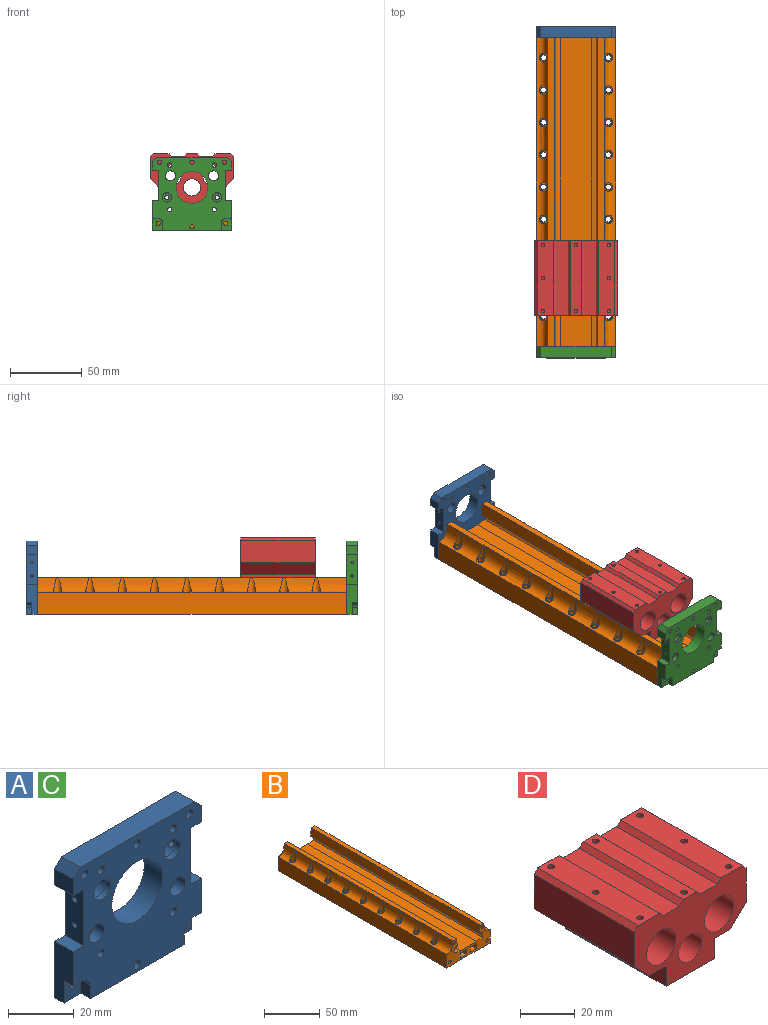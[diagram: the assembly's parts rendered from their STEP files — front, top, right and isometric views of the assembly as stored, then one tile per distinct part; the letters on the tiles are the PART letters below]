
ASSEMBLY  parts=4 mates=3
PART A: 53 faces, bbox 55x8x51 mm
  f0: cylinder r=3.25mm len=6.5mm, axis (0,-1,0), area 81mm2, adj f1,f19,f28,f29
  f1: plane 6.5x6.5mm, normal (0,-1,0), area 25.9mm2, adj f0,f5,f28,f29
  f2: cylinder r=4mm len=8mm, axis (0,1,0), area 148.1mm2, adj f20,f26,f27
  f3: plane 55x8mm, normal (0,0,-1), area 382mm2, adj f4,f19,f20,f23,f25,f33,f46,f48
  f4: plane 21x8mm, normal (1,0,0), area 135mm2, adj f3,f8,f19,f20,f24,f25
  f5: cylinder r=1.5mm len=4mm, axis (0,1,0), area 37.7mm2, adj f1,f20
  f6: cylinder r=1.5mm len=4mm, axis (0,1,0), area 37.7mm2, adj f20,f25
  f7: cylinder r=1.5mm len=8mm, axis (0,1,0), area 75.4mm2, adj f19,f20
  f8: plane 8x4.5mm, normal (0,0,1), area 36mm2, adj f4,f9,f19,f20
  f9: plane 21x8mm, normal (1,0,0), area 163.2mm2, adj f8,f10,f19,f20,f27,f29
  f10: plane 8x4.5mm, normal (0,0,-1), area 36mm2, adj f9,f11,f19,f20
  f11: plane 8x6mm, normal (1,0,0), area 48mm2, adj f10,f19,f20,f21
  f12: plane 49x8mm, normal (0,0,1), area 392mm2, adj f19,f20,f21,f44
  f13: cylinder r=1.5mm len=8mm, axis (0,1,0), area 75.4mm2, adj f19,f20
  f14: cylinder r=11mm len=22mm, axis (0,1,0), area 552.9mm2, adj f19,f20
  f15: cylinder r=1.5mm len=8mm, axis (0,1,0), area 75.4mm2, adj f19,f20
  f16: cylinder r=1.5mm len=8mm, axis (0,1,0), area 75.4mm2, adj f19,f20
  f17: cylinder r=1.5mm len=8mm, axis (0,1,0), area 75.4mm2, adj f19,f20
  f18: cylinder r=3.5mm len=7mm, axis (0,1,0), area 44mm2, adj f19,f26
  f19: plane 55x51mm, normal (0,-1,0), area 1911.9mm2, adj f0,f3,f4,f7,f8,f9,f10,f11
  f20: plane 55x51mm, normal (0,1,0), area 2041.5mm2, adj f2,f3,f4,f5,f6,f7,f8,f9
  f21: plane 8x3mm, normal (0.71,0,0.71), area 33.9mm2, adj f11,f12,f19,f20
  f22: cylinder r=3.25mm len=4mm, axis (0,-1,0), area 20.4mm2, adj f19,f23,f24,f25
  f23: plane 5x4mm, normal (1,0,0), area 20mm2, adj f3,f19,f22,f25
  f24: plane 4x4mm, normal (0,0,-1), area 16mm2, adj f4,f19,f22,f25
  f25: plane 8.25x7.25mm, normal (0,-1,0), area 50.5mm2, adj f3,f4,f6,f22,f23,f24
  f26: plane 8x8mm, normal (0,1,0), area 11.8mm2, adj f2,f18
  f27: cylinder r=0.88mm len=4.98mm, axis (1,0,0), area 24.6mm2, adj f2,f9
  f28: cone r=0mm half-angle=59deg, axis (1,0,0), area 2.6mm2, adj f0,f1,f29
  f29: cylinder r=0.88mm len=5mm, axis (1,0,0), area 26.9mm2, adj f0,f1,f9,f28
  f30: cylinder r=3.25mm len=6.5mm, axis (0,-1,0), area 81mm2, adj f19,f31,f51,f52
  f31: plane 6.5x6.5mm, normal (0,-1,0), area 25.9mm2, adj f30,f34,f51,f52
  f32: cylinder r=4mm len=8mm, axis (0,1,0), area 148.1mm2, adj f20,f49,f50
  f33: plane 21x8mm, normal (-1,0,0), area 135mm2, adj f3,f19,f20,f36,f47,f48
  f34: cylinder r=1.5mm len=4mm, axis (0,1,0), area 37.7mm2, adj f20,f31
  f35: cylinder r=1.5mm len=4mm, axis (0,1,0), area 37.7mm2, adj f20,f48
  f36: plane 8x4.5mm, normal (0,0,1), area 36mm2, adj f19,f20,f33,f37
  f37: plane 21x8mm, normal (-1,0,0), area 163.2mm2, adj f19,f20,f36,f38,f50,f52
  f38: plane 8x4.5mm, normal (0,0,-1), area 36mm2, adj f19,f20,f37,f39
  f39: plane 8x6mm, normal (-1,0,0), area 48mm2, adj f19,f20,f38,f44
  f40: cylinder r=1.5mm len=8mm, axis (0,1,0), area 75.4mm2, adj f19,f20
  f41: cylinder r=1.5mm len=8mm, axis (0,1,0), area 75.4mm2, adj f19,f20
  f42: cylinder r=1.5mm len=8mm, axis (0,1,0), area 75.4mm2, adj f19,f20
  f43: cylinder r=3.5mm len=7mm, axis (0,1,0), area 44mm2, adj f19,f49
  f44: plane 8x3mm, normal (-0.71,0,0.71), area 33.9mm2, adj f12,f19,f20,f39
  f45: cylinder r=3.25mm len=4mm, axis (0,-1,0), area 20.4mm2, adj f19,f46,f47,f48
  f46: plane 5x4mm, normal (-1,0,0), area 20mm2, adj f3,f19,f45,f48
  f47: plane 4x4mm, normal (0,0,-1), area 16mm2, adj f19,f33,f45,f48
  f48: plane 8.25x7.25mm, normal (0,-1,0), area 50.5mm2, adj f3,f33,f35,f45,f46,f47
  f49: plane 8x8mm, normal (0,1,0), area 11.8mm2, adj f32,f43
  f50: cylinder r=0.88mm len=4.98mm, axis (-1,0,0), area 24.6mm2, adj f32,f37
  f51: cone r=0mm half-angle=59deg, axis (-1,0,0), area 2.6mm2, adj f30,f31,f52
  f52: cylinder r=0.88mm len=5mm, axis (-1,0,0), area 26.9mm2, adj f30,f31,f37,f51
PART B: 142 faces, bbox 55x215x26 mm
  f0: cylinder r=3mm len=11mm, axis (0,0,-1), area 59.8mm2, adj f10,f46
  f1: cylinder r=3mm len=11mm, axis (0,0,-1), area 59.8mm2, adj f10,f45
  f2: cylinder r=3mm len=11mm, axis (0,0,-1), area 59.8mm2, adj f10,f43
  f3: cylinder r=3mm len=11mm, axis (0,0,-1), area 59.8mm2, adj f10,f41
  f4: cylinder r=3mm len=11mm, axis (0,0,-1), area 59.8mm2, adj f10,f39
  f5: cylinder r=3mm len=11mm, axis (0,0,-1), area 59.8mm2, adj f10,f37
  f6: cylinder r=3mm len=11mm, axis (0,0,-1), area 59.8mm2, adj f10,f35
  f7: cylinder r=3mm len=11mm, axis (0,0,-1), area 59.8mm2, adj f10,f33
  f8: cylinder r=3mm len=11mm, axis (0,0,-1), area 59.8mm2, adj f10,f29
  f9: cylinder r=1.5mm len=19.34mm, axis (0,1,0), area 173.6mm2, adj f27,f48
  f10: extruded ~215x11mm, area 2852.4mm2, adj f0,f1,f2,f3,f4,f5,f6,f7
  f11: plane 215x4.5mm, normal (0,0,1), area 967.5mm2, adj f10,f12,f27,f28
  f12: plane 215x8.5mm, normal (-0.99,0,0.12), area 1840.1mm2, adj f11,f13,f27,f28
  f13: plane 215x0.91mm, normal (0,0,-1), area 195.8mm2, adj f12,f14,f27,f28
  f14: cylinder r=3.56mm len=215mm, axis (0,1,0), area 1780.3mm2, adj f13,f15,f27,f28
  f15: plane 215x7mm, normal (-0.14,0,0.99), area 1520.3mm2, adj f14,f16,f27,f28
  f16: plane 215x21mm, normal (0,0,1), area 4515mm2, adj f15,f27,f28,f64
  f17: plane 215x35mm, normal (0,0,-1), area 7525mm2, adj f18,f27,f28,f65
  f18: plane 215x0.5mm, normal (-1,0,0), area 107.5mm2, adj f17,f19,f27,f28
  f19: plane 215x10mm, normal (0,0,-1), area 2036.9mm2, adj f18,f26,f27,f28,f30,f32,f34,f36
  f20: plane 215x6mm, normal (-1,0,0), area 1290mm2, adj f21,f23,f27,f28
  f21: plane 215x8mm, normal (0,0,1), area 1720mm2, adj f20,f22,f27,f28
  f22: plane 215x6mm, normal (1,0,0), area 1290mm2, adj f21,f23,f27,f28
  f23: plane 215x8mm, normal (0,0,-1), area 1720mm2, adj f20,f22,f27,f28
  f24: cylinder r=1.5mm len=215mm, axis (0,1,0), area 2026.3mm2, adj f27,f28
  f25: cylinder r=1.5mm len=12.34mm, axis (0,1,0), area 107.6mm2, adj f28,f31
  f26: plane 215x15mm, normal (1,0,0), area 3225mm2, adj f10,f19,f27,f28
  f27: plane 55x26mm, normal (0,-1,0), area 652.7mm2, adj f9,f10,f11,f12,f13,f14,f15,f16
  f28: plane 55x26mm, normal (0,1,0), area 652.7mm2, adj f10,f11,f12,f13,f14,f15,f16,f17
  f29: plane 6x6mm, normal (0,0,1), area 15.7mm2, adj f8,f30
  f30: cylinder r=2mm len=15mm, axis (0,0,-1), area 188.5mm2, adj f19,f29
  f31: cylinder r=3mm len=3mm, axis (0,0,-1), area 8mm2, adj f25
  f32: cylinder r=2mm len=15mm, axis (0,0,-1), area 188.5mm2, adj f19,f33
  f33: plane 6x6mm, normal (0,0,1), area 15.7mm2, adj f7,f32
  f34: cylinder r=2mm len=15mm, axis (0,0,-1), area 188.5mm2, adj f19,f35
  f35: plane 6x6mm, normal (0,0,1), area 15.7mm2, adj f6,f34
  f36: cylinder r=2mm len=15mm, axis (0,0,-1), area 188.5mm2, adj f19,f37
  f37: plane 6x6mm, normal (0,0,1), area 15.7mm2, adj f5,f36
  f38: cylinder r=2mm len=15mm, axis (0,0,-1), area 188.5mm2, adj f19,f39
  f39: plane 6x6mm, normal (0,0,1), area 15.7mm2, adj f4,f38
  f40: cylinder r=2mm len=15mm, axis (0,0,-1), area 188.5mm2, adj f19,f41
  f41: plane 6x6mm, normal (0,0,1), area 15.7mm2, adj f3,f40
  f42: cylinder r=2mm len=15mm, axis (0,0,-1), area 188.5mm2, adj f19,f43
  f43: plane 6x6mm, normal (0,0,1), area 15.7mm2, adj f2,f42
  f44: cylinder r=2mm len=15mm, axis (0,0,-1), area 188.5mm2, adj f19,f45
  f45: plane 6x6mm, normal (0,0,1), area 15.7mm2, adj f1,f44
  f46: plane 6x6mm, normal (0,0,1), area 15.7mm2, adj f0,f47
  f47: cylinder r=2mm len=15mm, axis (0,0,-1), area 188.5mm2, adj f19,f46
  f48: cylinder r=3mm len=3mm, axis (0,0,-1), area 8mm2, adj f9
  f49: cylinder r=3mm len=11mm, axis (0,0,-1), area 59.8mm2, adj f59,f91
  f50: cylinder r=3mm len=11mm, axis (0,0,-1), area 59.8mm2, adj f59,f90
  f51: cylinder r=3mm len=11mm, axis (0,0,-1), area 59.8mm2, adj f59,f88
  f52: cylinder r=3mm len=11mm, axis (0,0,-1), area 59.8mm2, adj f59,f86
  f53: cylinder r=3mm len=11mm, axis (0,0,-1), area 59.8mm2, adj f59,f84
  f54: cylinder r=3mm len=11mm, axis (0,0,-1), area 59.8mm2, adj f59,f82
  f55: cylinder r=3mm len=11mm, axis (0,0,-1), area 59.8mm2, adj f59,f80
  f56: cylinder r=3mm len=11mm, axis (0,0,-1), area 59.8mm2, adj f59,f78
  f57: cylinder r=3mm len=11mm, axis (0,0,-1), area 59.8mm2, adj f59,f74
  f58: cylinder r=1.5mm len=19.34mm, axis (0,1,0), area 173.6mm2, adj f27,f93
  f59: extruded ~215x11mm, area 2852.4mm2, adj f27,f28,f49,f50,f51,f52,f53,f54
  f60: plane 215x4.5mm, normal (0,0,1), area 967.5mm2, adj f27,f28,f59,f61
  f61: plane 215x8.5mm, normal (0.99,0,0.12), area 1840.1mm2, adj f27,f28,f60,f62
  f62: plane 215x0.91mm, normal (0,0,-1), area 195.8mm2, adj f27,f28,f61,f63
  f63: cylinder r=3.56mm len=215mm, axis (0,1,0), area 1780.3mm2, adj f27,f28,f62,f64
  f64: plane 215x7mm, normal (0.14,0,0.99), area 1520.3mm2, adj f16,f27,f28,f63
  f65: plane 215x0.5mm, normal (1,0,0), area 107.5mm2, adj f17,f27,f28,f66
  f66: plane 215x10mm, normal (0,0,-1), area 2036.9mm2, adj f27,f28,f65,f73,f75,f77,f79,f81
  f67: plane 215x6mm, normal (1,0,0), area 1290mm2, adj f27,f28,f68,f70
  f68: plane 215x8mm, normal (0,0,1), area 1720mm2, adj f27,f28,f67,f69
  f69: plane 215x6mm, normal (-1,0,0), area 1290mm2, adj f27,f28,f68,f70
  f70: plane 215x8mm, normal (0,0,-1), area 1720mm2, adj f27,f28,f67,f69
  f71: cylinder r=1.5mm len=215mm, axis (0,1,0), area 2026.3mm2, adj f27,f28
  f72: cylinder r=1.5mm len=12.34mm, axis (0,1,0), area 107.6mm2, adj f28,f76
  f73: plane 215x15mm, normal (-1,0,0), area 3225mm2, adj f27,f28,f59,f66
  f74: plane 6x6mm, normal (0,0,1), area 15.7mm2, adj f57,f75
  f75: cylinder r=2mm len=15mm, axis (0,0,-1), area 188.5mm2, adj f66,f74
  f76: cylinder r=3mm len=3mm, axis (0,0,-1), area 8mm2, adj f72
  f77: cylinder r=2mm len=15mm, axis (0,0,-1), area 188.5mm2, adj f66,f78
  f78: plane 6x6mm, normal (0,0,1), area 15.7mm2, adj f56,f77
  f79: cylinder r=2mm len=15mm, axis (0,0,-1), area 188.5mm2, adj f66,f80
  f80: plane 6x6mm, normal (0,0,1), area 15.7mm2, adj f55,f79
  f81: cylinder r=2mm len=15mm, axis (0,0,-1), area 188.5mm2, adj f66,f82
  f82: plane 6x6mm, normal (0,0,1), area 15.7mm2, adj f54,f81
  f83: cylinder r=2mm len=15mm, axis (0,0,-1), area 188.5mm2, adj f66,f84
  f84: plane 6x6mm, normal (0,0,1), area 15.7mm2, adj f53,f83
  f85: cylinder r=2mm len=15mm, axis (0,0,-1), area 188.5mm2, adj f66,f86
  f86: plane 6x6mm, normal (0,0,1), area 15.7mm2, adj f52,f85
  f87: cylinder r=2mm len=15mm, axis (0,0,-1), area 188.5mm2, adj f66,f88
  f88: plane 6x6mm, normal (0,0,1), area 15.7mm2, adj f51,f87
  f89: cylinder r=2mm len=15mm, axis (0,0,-1), area 188.5mm2, adj f66,f90
  f90: plane 6x6mm, normal (0,0,1), area 15.7mm2, adj f50,f89
  f91: plane 6x6mm, normal (0,0,1), area 15.7mm2, adj f49,f92
  f92: cylinder r=2mm len=15mm, axis (0,0,-1), area 188.5mm2, adj f66,f91
  f93: cylinder r=3mm len=3mm, axis (0,0,-1), area 8mm2, adj f58
  f94: cylinder r=3mm len=3mm, axis (0,0,-1), area 8mm2, adj f96
  f95: cylinder r=3mm len=3mm, axis (0,0,-1), area 8mm2, adj f96
  f96: cylinder r=1.5mm len=19.18mm, axis (0,1,0), area 163.4mm2, adj f94,f95
  f97: cylinder r=3mm len=3mm, axis (0,0,-1), area 8mm2, adj f99
  f98: cylinder r=3mm len=3mm, axis (0,0,-1), area 8mm2, adj f99
  f99: cylinder r=1.5mm len=19.18mm, axis (0,1,0), area 163.4mm2, adj f97,f98
  f100: cylinder r=3mm len=3mm, axis (0,0,-1), area 8mm2, adj f102
  f101: cylinder r=3mm len=3mm, axis (0,0,-1), area 8mm2, adj f102
  f102: cylinder r=1.5mm len=19.18mm, axis (0,1,0), area 163.4mm2, adj f100,f101
  f103: cylinder r=3mm len=3mm, axis (0,0,-1), area 8mm2, adj f105
  f104: cylinder r=3mm len=3mm, axis (0,0,-1), area 8mm2, adj f105
  f105: cylinder r=1.5mm len=19.18mm, axis (0,1,0), area 163.4mm2, adj f103,f104
  f106: cylinder r=3mm len=3mm, axis (0,0,-1), area 8mm2, adj f108
  f107: cylinder r=3mm len=3mm, axis (0,0,-1), area 8mm2, adj f108
  f108: cylinder r=1.5mm len=19.18mm, axis (0,1,0), area 163.4mm2, adj f106,f107
  f109: cylinder r=3mm len=3mm, axis (0,0,-1), area 8mm2, adj f111
  f110: cylinder r=3mm len=3mm, axis (0,0,-1), area 8mm2, adj f111
  f111: cylinder r=1.5mm len=19.18mm, axis (0,1,0), area 163.4mm2, adj f109,f110
  f112: cylinder r=3mm len=3mm, axis (0,0,-1), area 8mm2, adj f114
  f113: cylinder r=3mm len=3mm, axis (0,0,-1), area 8mm2, adj f114
  f114: cylinder r=1.5mm len=19.18mm, axis (0,1,0), area 163.4mm2, adj f112,f113
  f115: cylinder r=3mm len=3mm, axis (0,0,-1), area 8mm2, adj f117
  f116: cylinder r=3mm len=3mm, axis (0,0,-1), area 8mm2, adj f117
  f117: cylinder r=1.5mm len=19.18mm, axis (0,1,0), area 163.4mm2, adj f115,f116
  f118: cylinder r=3mm len=3mm, axis (0,0,-1), area 8mm2, adj f120
  f119: cylinder r=3mm len=3mm, axis (0,0,-1), area 8mm2, adj f120
  f120: cylinder r=1.5mm len=19.18mm, axis (0,1,0), area 163.4mm2, adj f118,f119
  f121: cylinder r=3mm len=3mm, axis (0,0,-1), area 8mm2, adj f123
  f122: cylinder r=3mm len=3mm, axis (0,0,-1), area 8mm2, adj f123
  f123: cylinder r=1.5mm len=19.18mm, axis (0,1,0), area 163.4mm2, adj f121,f122
  f124: cylinder r=3mm len=3mm, axis (0,0,-1), area 8mm2, adj f126
  f125: cylinder r=3mm len=3mm, axis (0,0,-1), area 8mm2, adj f126
  f126: cylinder r=1.5mm len=19.18mm, axis (0,1,0), area 163.4mm2, adj f124,f125
  f127: cylinder r=3mm len=3mm, axis (0,0,-1), area 8mm2, adj f129
  f128: cylinder r=3mm len=3mm, axis (0,0,-1), area 8mm2, adj f129
  f129: cylinder r=1.5mm len=19.18mm, axis (0,1,0), area 163.4mm2, adj f127,f128
  f130: cylinder r=3mm len=3mm, axis (0,0,-1), area 8mm2, adj f132
  f131: cylinder r=3mm len=3mm, axis (0,0,-1), area 8mm2, adj f132
  f132: cylinder r=1.5mm len=19.18mm, axis (0,1,0), area 163.4mm2, adj f130,f131
  f133: cylinder r=3mm len=3mm, axis (0,0,-1), area 8mm2, adj f135
  f134: cylinder r=3mm len=3mm, axis (0,0,-1), area 8mm2, adj f135
  f135: cylinder r=1.5mm len=19.18mm, axis (0,1,0), area 163.4mm2, adj f133,f134
  f136: cylinder r=3mm len=3mm, axis (0,0,-1), area 8mm2, adj f138
  f137: cylinder r=3mm len=3mm, axis (0,0,-1), area 8mm2, adj f138
  f138: cylinder r=1.5mm len=19.18mm, axis (0,1,0), area 163.4mm2, adj f136,f137
  f139: cylinder r=3mm len=3mm, axis (0,0,-1), area 8mm2, adj f141
  f140: cylinder r=3mm len=3mm, axis (0,0,-1), area 8mm2, adj f141
  f141: cylinder r=1.5mm len=19.18mm, axis (0,1,0), area 163.4mm2, adj f139,f140
PART C: same geometry as A
PART D: 41 faces, bbox 58x52x34.5 mm
  f0: plane 52x7mm, normal (0,0,1), area 354.2mm2, adj f9,f10,f14,f22,f24,f34
  f1: cylinder r=6mm len=52mm, axis (0,1,0), area 1960.4mm2, adj f9,f10
  f2: plane 52x25mm, normal (0,0,-1), area 1300mm2, adj f3,f9,f10,f25
  f3: plane 52x9mm, normal (1,0,0), area 468mm2, adj f2,f4,f9,f10
  f4: plane 52x8.5mm, normal (0,0,-1), area 442mm2, adj f3,f9,f10,f11
  f5: plane 52x15.5mm, normal (1,0,0), area 806mm2, adj f9,f10,f11,f12
  f6: plane 52x11mm, normal (0,0,1), area 557.3mm2, adj f9,f10,f12,f13,f16,f18,f20
  f7: plane 52x8.5mm, normal (0,0,1), area 442mm2, adj f9,f10,f13,f14
  f8: cylinder r=7.5mm len=52mm, axis (0,1,0), area 2450.4mm2, adj f9,f10
  f9: plane 58x34.5mm, normal (0,-1,0), area 1127.5mm2, adj f0,f1,f2,f3,f4,f5,f6,f7
  f10: plane 58x34.5mm, normal (0,1,0), area 1127.5mm2, adj f0,f1,f2,f3,f4,f5,f6,f7
  f11: plane 52x8mm, normal (0.71,0,-0.71), area 588.3mm2, adj f4,f5,f9,f10
  f12: plane 52x2mm, normal (0.71,0,0.71), area 147.1mm2, adj f5,f6,f9,f10
  f13: plane 52x2mm, normal (-0.71,0,0.71), area 147.1mm2, adj f6,f7,f9,f10
  f14: plane 52x2mm, normal (0.71,0,0.71), area 147.1mm2, adj f0,f7,f9,f10
  f15: cone r=0mm half-angle=59deg, axis (0,0,1), area 5.7mm2, adj f16
  f16: cylinder r=1.25mm len=10.75mm, axis (0,0,1), area 84.4mm2, adj f6,f15
  f17: cone r=0mm half-angle=59deg, axis (0,0,1), area 5.7mm2, adj f18
  f18: cylinder r=1.25mm len=10.75mm, axis (0,0,1), area 84.4mm2, adj f6,f17
  f19: cone r=0mm half-angle=59deg, axis (0,0,1), area 5.7mm2, adj f20
  f20: cylinder r=1.25mm len=10.75mm, axis (0,0,1), area 84.4mm2, adj f6,f19
  f21: cone r=0mm half-angle=59deg, axis (0,0,1), area 5.7mm2, adj f22
  f22: cylinder r=1.25mm len=10.75mm, axis (0,0,1), area 84.4mm2, adj f0,f21
  f23: cone r=0mm half-angle=59deg, axis (0,0,1), area 5.7mm2, adj f24
  f24: cylinder r=1.25mm len=10.75mm, axis (0,0,1), area 84.4mm2, adj f0,f23
  f25: plane 52x9mm, normal (-1,0,0), area 468mm2, adj f2,f9,f10,f26
  f26: plane 52x8.5mm, normal (0,0,-1), area 442mm2, adj f9,f10,f25,f31
  f27: plane 52x15.5mm, normal (-1,0,0), area 806mm2, adj f9,f10,f31,f32
  f28: plane 52x11mm, normal (0,0,1), area 557.3mm2, adj f9,f10,f32,f33,f36,f38,f40
  f29: plane 52x8.5mm, normal (0,0,1), area 442mm2, adj f9,f10,f33,f34
  f30: cylinder r=7.5mm len=52mm, axis (0,1,0), area 2450.4mm2, adj f9,f10
  f31: plane 52x8mm, normal (-0.71,0,-0.71), area 588.3mm2, adj f9,f10,f26,f27
  f32: plane 52x2mm, normal (-0.71,0,0.71), area 147.1mm2, adj f9,f10,f27,f28
  f33: plane 52x2mm, normal (0.71,0,0.71), area 147.1mm2, adj f9,f10,f28,f29
  f34: plane 52x2mm, normal (-0.71,0,0.71), area 147.1mm2, adj f0,f9,f10,f29
  f35: cone r=0mm half-angle=59deg, axis (0,0,1), area 5.7mm2, adj f36
  f36: cylinder r=1.25mm len=10.75mm, axis (0,0,1), area 84.4mm2, adj f28,f35
  f37: cone r=0mm half-angle=59deg, axis (0,0,1), area 5.7mm2, adj f38
  f38: cylinder r=1.25mm len=10.75mm, axis (0,0,1), area 84.4mm2, adj f28,f37
  f39: cone r=0mm half-angle=59deg, axis (0,0,1), area 5.7mm2, adj f40
  f40: cylinder r=1.25mm len=10.75mm, axis (0,0,1), area 84.4mm2, adj f28,f39
PLACE A rot(axis=(0,0,1),180deg) t=(0,107.5,0)mm
PLACE B at identity fixed
PLACE C t=(0,-107.5,0)mm
PLACE D t=(0,-59.86,17)mm
MATE fastened A.f20 <-> B.f28  axis (0,-1,0) through (27.5,107.5,-13)mm
MATE slider C.f2 <-> D.f8  axis (0,1,0) through (15,-107.5,25)mm
MATE fastened C.f20 <-> B.f27  axis (0,1,0) through (27.5,-107.5,-13)mm
